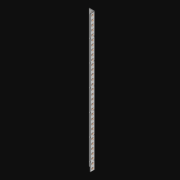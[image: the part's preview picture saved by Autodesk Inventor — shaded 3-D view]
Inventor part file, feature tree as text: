
AUTODESK INVENTOR PART (.ipt)
format: ipt  version: 2021 (Build 250183000, 183)  size: 1,311,232 bytes
history: native  units: in
note: dims shown in document units (in); Inventor stores cm internally (conversion verified against a paired STEP export)
features: extrude x66, other x64, sketch x4, pattern_linear x2, sheet_metal_op x1
ambient origin geometry x8: Origin, YZ Plane, XZ Plane, XY Plane, X Axis, Y Axis, Z Axis, Center Point
bodies: Solid1 (feature_tree)
feature tree (137):
  pattern_linear  "Rectangular Pattern1"  Spacing1=0.5in  [1 undecoded]
  pattern_linear  "Rectangular Pattern3"  Count1=32  [1 undecoded]
  extrude  "Extrusion1"  Depth=0.5in
  extrude  "Extrusion2"  Depth=0.5in
  sketch  "Sketch1"  dims[d0=0.182in]
  other  "Srf1"
  sketch  "Sketch3"  dims[d1=0.063in d2=0.0in]
  other  "Srf3"
  other  "Srf4"
  other  "Srf5"
  other  "Srf6"
  other  "Srf7"
  other  "Srf8"
  other  "Srf9"
  other  "Srf10"
  other  "Srf11"
  other  "Srf12"
  other  "Srf13"
  other  "Srf14"
  other  "Srf15"
  other  "Srf16"
  other  "Srf17"
  other  "Srf18"
  other  "Srf19"
  other  "Srf20"
  other  "Srf21"
  other  "Srf22"
  other  "Srf23"
  other  "Srf24"
  other  "Srf25"
  other  "Srf26"
  other  "Srf27"
  other  "Srf28"
  other  "Srf29"
  other  "Srf30"
  other  "Srf31"
  other  "Srf32"
  other  "Srf33"
  other  "Srf34"
  other  "Srf142"
  other  "Srf143"
  other  "Srf144"
  other  "Srf145"
  other  "Srf146"
  other  "Srf147"
  other  "Srf148"
  other  "Srf149"
  other  "Srf150"
  other  "Srf151"
  other  "Srf152"
  other  "Srf153"
  other  "Srf154"
  other  "Srf155"
  other  "Srf156"
  other  "Srf157"
  other  "Srf158"
  other  "Srf159"
  other  "Srf160"
  other  "Srf161"
  other  "Srf162"
  other  "Srf163"
  other  "Srf164"
  other  "Srf165"
  other  "Srf166"
  other  "Srf167"
  other  "Srf168"
  other  "Srf169"
  other  "Srf170"
  other  "Srf171"
  other  "Srf172"
  sketch  "Sketch4"  dims[d6=0.182in]
  sketch  "Sketch5"  dims[d7=0.063in d8=0.0in d11=0.5in d12=0.3937in d14=0.5in d18=12.5984in d20=0.5in d21=1.5in d22=0.0in d23=0.841in d24=0.0in]
  sheet_metal_op  "Fold1"
  extrude  "ExtrusionSrf1"  TaperAngle=0.0deg  [1 undecoded]
  extrude  "ExtrusionSrf3"  Depth=0.5in TaperAngle=0.0deg
  extrude  "ExtrusionSrf4"  [1 undecoded]
  extrude  "ExtrusionSrf5"  [1 undecoded]
  extrude  "ExtrusionSrf6"  [1 undecoded]
  extrude  "ExtrusionSrf7"  [1 undecoded]
  extrude  "ExtrusionSrf8"  [1 undecoded]
  extrude  "ExtrusionSrf9"  [1 undecoded]
  extrude  "ExtrusionSrf10"  [1 undecoded]
  extrude  "ExtrusionSrf11"  [1 undecoded]
  extrude  "ExtrusionSrf12"  [1 undecoded]
  extrude  "ExtrusionSrf13"  [1 undecoded]
  extrude  "ExtrusionSrf14"  [1 undecoded]
  extrude  "ExtrusionSrf15"  [1 undecoded]
  extrude  "ExtrusionSrf16"  [1 undecoded]
  extrude  "ExtrusionSrf17"  [1 undecoded]
  extrude  "ExtrusionSrf18"  [1 undecoded]
  extrude  "ExtrusionSrf19"  [1 undecoded]
  extrude  "ExtrusionSrf20"  [1 undecoded]
  extrude  "ExtrusionSrf21"  [1 undecoded]
  extrude  "ExtrusionSrf22"  [1 undecoded]
  extrude  "ExtrusionSrf23"  [1 undecoded]
  extrude  "ExtrusionSrf24"  [1 undecoded]
  extrude  "ExtrusionSrf25"  [1 undecoded]
  extrude  "ExtrusionSrf26"  [1 undecoded]
  extrude  "ExtrusionSrf27"  [1 undecoded]
  extrude  "ExtrusionSrf28"  [1 undecoded]
  extrude  "ExtrusionSrf29"  [1 undecoded]
  extrude  "ExtrusionSrf30"  [1 undecoded]
  extrude  "ExtrusionSrf31"  [1 undecoded]
  extrude  "ExtrusionSrf32"  [1 undecoded]
  extrude  "ExtrusionSrf33"  [1 undecoded]
  extrude  "ExtrusionSrf34"  [1 undecoded]
  extrude  "ExtrusionSrf142"  [1 undecoded]
  extrude  "ExtrusionSrf143"  [1 undecoded]
  extrude  "ExtrusionSrf144"  [1 undecoded]
  extrude  "ExtrusionSrf145"  [1 undecoded]
  extrude  "ExtrusionSrf146"  [1 undecoded]
  extrude  "ExtrusionSrf147"  [1 undecoded]
  extrude  "ExtrusionSrf148"  [1 undecoded]
  extrude  "ExtrusionSrf149"  [1 undecoded]
  extrude  "ExtrusionSrf150"  [1 undecoded]
  extrude  "ExtrusionSrf151"  [1 undecoded]
  extrude  "ExtrusionSrf152"  [1 undecoded]
  extrude  "ExtrusionSrf153"  [1 undecoded]
  extrude  "ExtrusionSrf154"  [1 undecoded]
  extrude  "ExtrusionSrf155"  [1 undecoded]
  extrude  "ExtrusionSrf156"  [1 undecoded]
  extrude  "ExtrusionSrf157"  [1 undecoded]
  extrude  "ExtrusionSrf158"  [1 undecoded]
  extrude  "ExtrusionSrf159"  [1 undecoded]
  extrude  "ExtrusionSrf160"  [1 undecoded]
  extrude  "ExtrusionSrf161"  [1 undecoded]
  extrude  "ExtrusionSrf162"  [1 undecoded]
  extrude  "ExtrusionSrf163"  [1 undecoded]
  extrude  "ExtrusionSrf164"  [1 undecoded]
  extrude  "ExtrusionSrf165"  [1 undecoded]
  extrude  "ExtrusionSrf166"  [1 undecoded]
  extrude  "ExtrusionSrf167"  [1 undecoded]
  extrude  "ExtrusionSrf168"  [1 undecoded]
  extrude  "ExtrusionSrf169"  [1 undecoded]
  extrude  "ExtrusionSrf170"  [1 undecoded]
  extrude  "ExtrusionSrf171"  [1 undecoded]
  extrude  "ExtrusionSrf172"  [1 undecoded]
note: 65 required parameter values undecoded (feature->parameter linkage not recoverable at this tier; creation-order binding heuristic only, values carry confidence <= 0.55)
